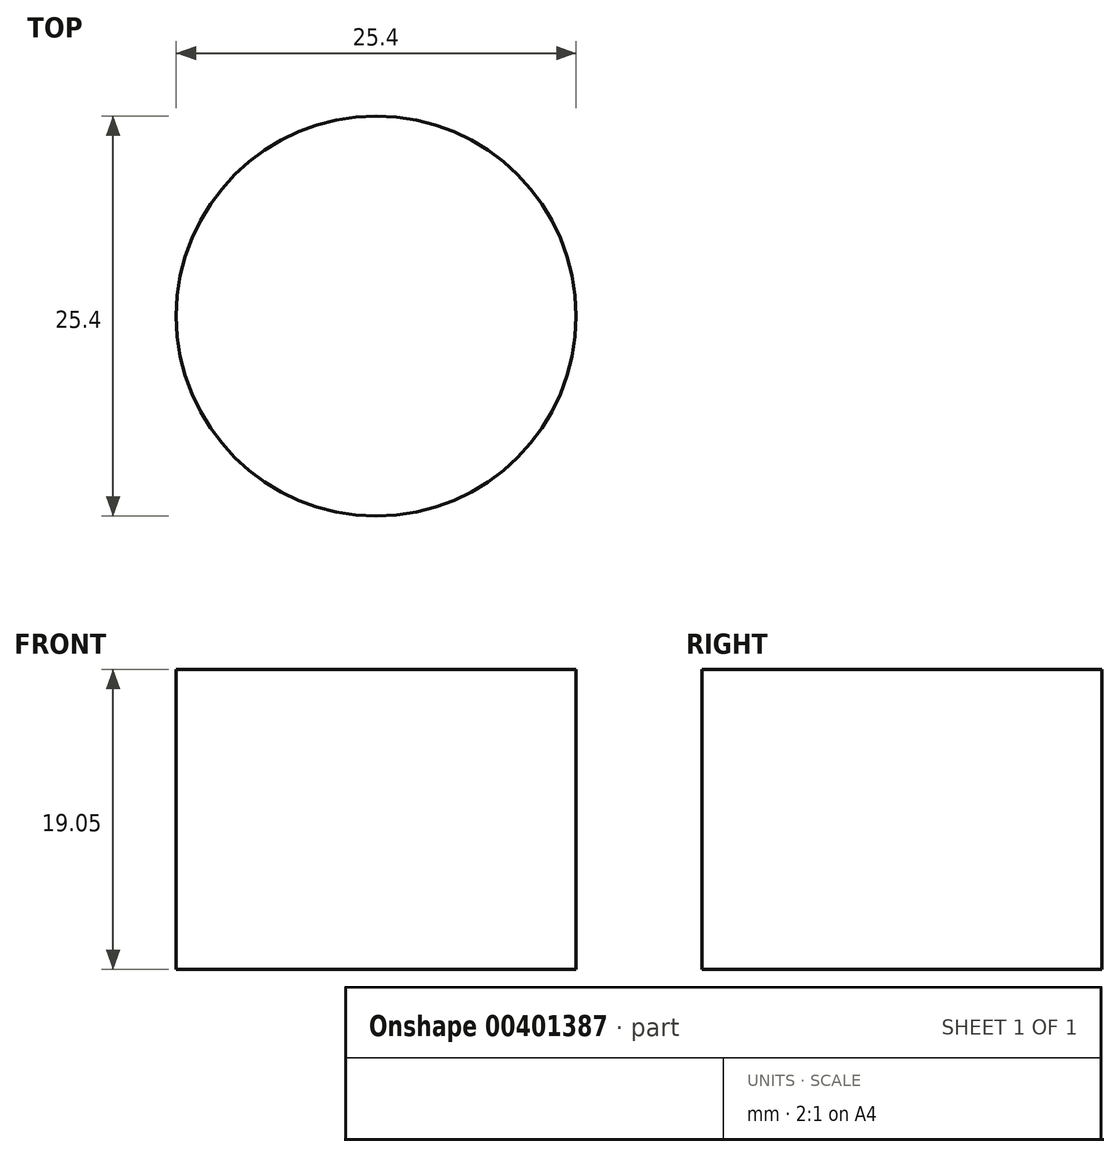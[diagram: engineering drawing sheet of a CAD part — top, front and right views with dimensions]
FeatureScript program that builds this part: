
annotation { "Feature Type Name" : "Feature", "Feature Type Description" : "" }
export const myFeature = defineFeature(function(context is Context, id is Id, definition is map)
    precondition{}
    {
        {
            var Q0;
            Q0=qCreatedBy(makeId("Top.planeOp"),FACE);
            var sketch = newSketch(context, id + "F0", { "sketchPlane" : qUnion([Q0])});
            skCircle(sketch, "E0", {"center": v(0, 0) * mm, "radius": 12.7 * mm});
            skSolve(sketch);
        }
        {
            var Q0;
            Q0=qSketchRegion(id+"F0",true);
            extrude(context, id + "F1", {"entities" : qUnion([Q0]), "depth" : 19.05 * mm});
        }
    });
